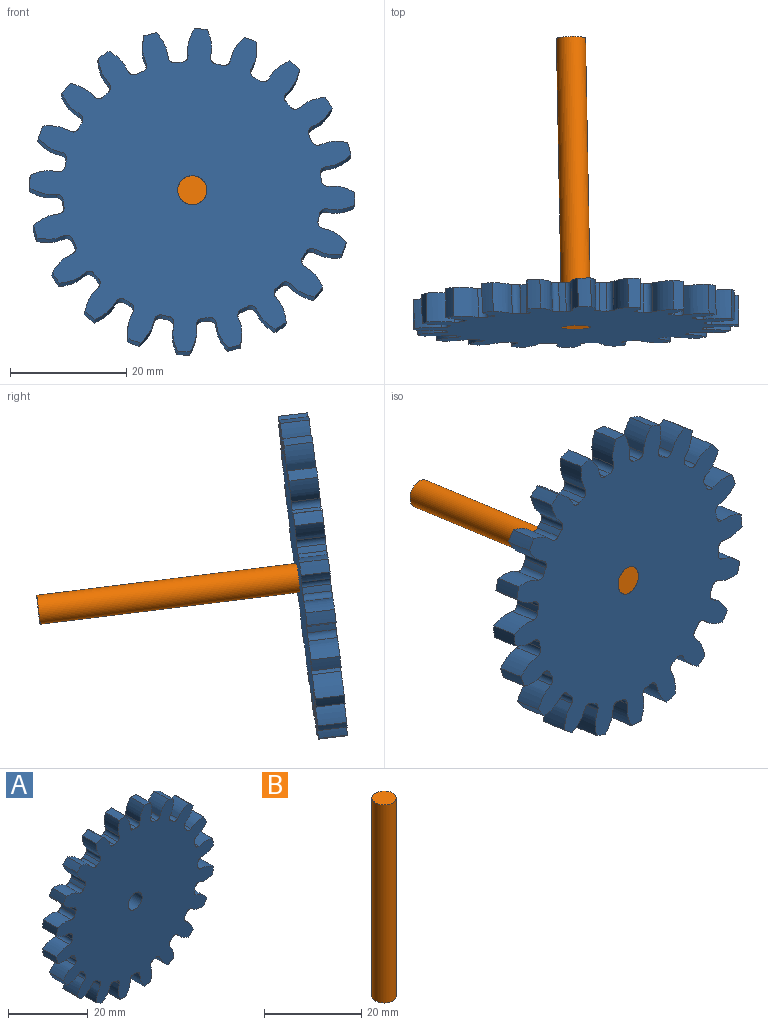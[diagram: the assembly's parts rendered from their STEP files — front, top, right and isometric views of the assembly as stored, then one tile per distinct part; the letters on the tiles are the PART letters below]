
ASSEMBLY  parts=2 mates=1
PART A: 123 faces, bbox 55.6x5x55.6 mm
  f0: extruded ~5x4.52mm, area 24.4mm2, adj f80,f81,f82,f83
  f1: cylinder r=22.23mm len=5mm, axis (0,1,0), area 5.9mm2, adj f81,f82,f83,f84
  f2: extruded ~5x4.52mm, area 24.4mm2, adj f3,f81,f82,f84
  f3: cylinder r=27.94mm len=5mm, axis (0,1,0), area 11.2mm2, adj f2,f4,f81,f82
  f4: extruded ~5x4.78mm, area 24.4mm2, adj f3,f81,f82,f85
  f5: cylinder r=22.23mm len=5mm, axis (0,1,0), area 5.9mm2, adj f81,f82,f85,f86
  f6: extruded ~5x3.82mm, area 24.4mm2, adj f7,f81,f82,f86
  f7: cylinder r=27.94mm len=5mm, axis (0,1,0), area 11.2mm2, adj f6,f8,f81,f82
  f8: extruded ~5x4.57mm, area 24.4mm2, adj f7,f81,f82,f87
  f9: cylinder r=22.23mm len=5mm, axis (0,1,0), area 5.9mm2, adj f81,f82,f87,f88
  f10: extruded ~5x3.92mm, area 24.4mm2, adj f11,f81,f82,f88
  f11: cylinder r=27.94mm len=5mm, axis (0,1,0), area 11.2mm2, adj f10,f12,f81,f82
  f12: extruded ~5x3.92mm, area 24.4mm2, adj f11,f81,f82,f89
  f13: cylinder r=22.23mm len=5mm, axis (0,1,0), area 5.9mm2, adj f81,f82,f89,f90
  f14: extruded ~5x4.57mm, area 24.4mm2, adj f15,f81,f82,f90
  f15: cylinder r=27.94mm len=5mm, axis (0,1,0), area 11.2mm2, adj f14,f16,f81,f82
  f16: extruded ~5x3.82mm, area 24.4mm2, adj f15,f81,f82,f91
  f17: cylinder r=22.23mm len=5mm, axis (0,1,0), area 5.9mm2, adj f81,f82,f91,f92
  f18: extruded ~5x4.78mm, area 24.4mm2, adj f19,f81,f82,f92
  f19: cylinder r=27.94mm len=5mm, axis (0,1,0), area 11.2mm2, adj f18,f20,f81,f82
  f20: extruded ~5x4.52mm, area 24.4mm2, adj f19,f81,f82,f93
  f21: cylinder r=22.23mm len=5mm, axis (0,1,0), area 5.9mm2, adj f81,f82,f93,f94
  f22: extruded ~5x4.52mm, area 24.4mm2, adj f23,f81,f82,f94
  f23: cylinder r=27.94mm len=5mm, axis (0,1,0), area 11.2mm2, adj f22,f24,f81,f82
  f24: extruded ~5x4.78mm, area 24.4mm2, adj f23,f81,f82,f95
  f25: cylinder r=22.23mm len=5mm, axis (0,1,0), area 5.9mm2, adj f81,f82,f95,f96
  f26: extruded ~5x3.82mm, area 24.4mm2, adj f27,f81,f82,f96
  f27: cylinder r=27.94mm len=5mm, axis (0,1,0), area 11.2mm2, adj f26,f28,f81,f82
  f28: extruded ~5x4.57mm, area 24.4mm2, adj f27,f81,f82,f97
  f29: cylinder r=22.23mm len=5mm, axis (0,1,0), area 5.9mm2, adj f81,f82,f97,f98
  f30: extruded ~5x3.92mm, area 24.4mm2, adj f31,f81,f82,f98
  f31: cylinder r=27.94mm len=5mm, axis (0,1,0), area 11.2mm2, adj f30,f32,f81,f82
  f32: extruded ~5x3.92mm, area 24.4mm2, adj f31,f81,f82,f99
  f33: cylinder r=22.23mm len=5mm, axis (0,1,0), area 5.9mm2, adj f81,f82,f99,f100
  f34: extruded ~5x4.57mm, area 24.4mm2, adj f35,f81,f82,f100
  f35: cylinder r=27.94mm len=5mm, axis (0,1,0), area 11.2mm2, adj f34,f36,f81,f82
  f36: extruded ~5x3.82mm, area 24.4mm2, adj f35,f81,f82,f101
  f37: cylinder r=22.23mm len=5mm, axis (0,1,0), area 5.9mm2, adj f81,f82,f101,f102
  f38: extruded ~5x4.78mm, area 24.4mm2, adj f39,f81,f82,f102
  f39: cylinder r=27.94mm len=5mm, axis (0,1,0), area 11.2mm2, adj f38,f40,f81,f82
  f40: extruded ~5x4.52mm, area 24.4mm2, adj f39,f81,f82,f103
  f41: cylinder r=22.23mm len=5mm, axis (0,1,0), area 5.9mm2, adj f81,f82,f103,f104
  f42: extruded ~5x4.52mm, area 24.4mm2, adj f43,f81,f82,f104
  f43: cylinder r=27.94mm len=5mm, axis (0,1,0), area 11.2mm2, adj f42,f44,f81,f82
  f44: extruded ~5x4.78mm, area 24.4mm2, adj f43,f81,f82,f105
  f45: cylinder r=22.23mm len=5mm, axis (0,1,0), area 5.9mm2, adj f81,f82,f105,f106
  f46: extruded ~5x3.82mm, area 24.4mm2, adj f47,f81,f82,f106
  f47: cylinder r=27.94mm len=5mm, axis (0,1,0), area 11.2mm2, adj f46,f48,f81,f82
  f48: extruded ~5x4.57mm, area 24.4mm2, adj f47,f81,f82,f107
  f49: cylinder r=22.23mm len=5mm, axis (0,1,0), area 5.9mm2, adj f81,f82,f107,f108
  f50: extruded ~5x3.92mm, area 24.4mm2, adj f51,f81,f82,f108
  f51: cylinder r=27.94mm len=5mm, axis (0,1,0), area 11.2mm2, adj f50,f52,f81,f82
  f52: extruded ~5x3.92mm, area 24.4mm2, adj f51,f81,f82,f109
  f53: cylinder r=22.23mm len=5mm, axis (0,1,0), area 5.9mm2, adj f81,f82,f109,f110
  f54: extruded ~5x4.57mm, area 24.4mm2, adj f55,f81,f82,f110
  f55: cylinder r=27.94mm len=5mm, axis (0,1,0), area 11.2mm2, adj f54,f56,f81,f82
  f56: extruded ~5x3.82mm, area 24.4mm2, adj f55,f81,f82,f111
  f57: cylinder r=22.23mm len=5mm, axis (0,1,0), area 5.9mm2, adj f81,f82,f111,f112
  f58: extruded ~5x4.78mm, area 24.4mm2, adj f59,f81,f82,f112
  f59: cylinder r=27.94mm len=5mm, axis (0,1,0), area 11.2mm2, adj f58,f60,f81,f82
  f60: extruded ~5x4.52mm, area 24.4mm2, adj f59,f81,f82,f113
  f61: cylinder r=22.23mm len=5mm, axis (0,1,0), area 5.9mm2, adj f81,f82,f113,f114
  f62: extruded ~5x4.52mm, area 24.4mm2, adj f63,f81,f82,f114
  f63: cylinder r=27.94mm len=5mm, axis (0,1,0), area 11.2mm2, adj f62,f64,f81,f82
  f64: extruded ~5x4.78mm, area 24.4mm2, adj f63,f81,f82,f115
  f65: cylinder r=22.23mm len=5mm, axis (0,1,0), area 5.9mm2, adj f81,f82,f115,f116
  f66: extruded ~5x3.82mm, area 24.4mm2, adj f67,f81,f82,f116
  f67: cylinder r=27.94mm len=5mm, axis (0,1,0), area 11.2mm2, adj f66,f68,f81,f82
  f68: extruded ~5x4.57mm, area 24.4mm2, adj f67,f81,f82,f117
  f69: cylinder r=22.23mm len=5mm, axis (0,1,0), area 5.9mm2, adj f81,f82,f117,f118
  f70: extruded ~5x3.92mm, area 24.4mm2, adj f71,f81,f82,f118
  f71: cylinder r=27.94mm len=5mm, axis (0,1,0), area 11.2mm2, adj f70,f72,f81,f82
  f72: extruded ~5x3.92mm, area 24.4mm2, adj f71,f81,f82,f119
  f73: cylinder r=22.23mm len=5mm, axis (0,1,0), area 5.9mm2, adj f81,f82,f119,f120
  f74: extruded ~5x4.57mm, area 24.4mm2, adj f75,f81,f82,f120
  f75: cylinder r=27.94mm len=5mm, axis (0,1,0), area 11.2mm2, adj f74,f76,f81,f82
  f76: extruded ~5x3.82mm, area 24.4mm2, adj f75,f81,f82,f121
  f77: cylinder r=22.23mm len=5mm, axis (0,1,0), area 5.9mm2, adj f81,f82,f121,f122
  f78: extruded ~5x4.78mm, area 24.4mm2, adj f80,f81,f82,f122
  f79: cylinder r=2.5mm len=5mm, axis (0,1,0), area 78.5mm2, adj f81,f82
  f80: cylinder r=27.94mm len=5mm, axis (0,1,0), area 11.2mm2, adj f0,f78,f81,f82
  f81: plane 55.58x55.58mm, normal (0,-1,0), area 1957.9mm2, adj f0,f1,f2,f3,f4,f5,f6,f7
  f82: plane 55.58x55.58mm, normal (0,1,0), area 1957.9mm2, adj f0,f1,f2,f3,f4,f5,f6,f7
  f83: cylinder r=1.09mm len=5mm, axis (0,1,0), area 8.3mm2, adj f0,f1,f81,f82
  f84: cylinder r=1.09mm len=5mm, axis (0,1,0), area 8.3mm2, adj f1,f2,f81,f82
  f85: cylinder r=1.09mm len=5mm, axis (0,1,0), area 8.3mm2, adj f4,f5,f81,f82
  f86: cylinder r=1.09mm len=5mm, axis (0,1,0), area 8.3mm2, adj f5,f6,f81,f82
  f87: cylinder r=1.09mm len=5mm, axis (0,1,0), area 8.3mm2, adj f8,f9,f81,f82
  f88: cylinder r=1.09mm len=5mm, axis (0,1,0), area 8.3mm2, adj f9,f10,f81,f82
  f89: cylinder r=1.09mm len=5mm, axis (0,1,0), area 8.3mm2, adj f12,f13,f81,f82
  f90: cylinder r=1.09mm len=5mm, axis (0,1,0), area 8.3mm2, adj f13,f14,f81,f82
  f91: cylinder r=1.09mm len=5mm, axis (0,1,0), area 8.3mm2, adj f16,f17,f81,f82
  f92: cylinder r=1.09mm len=5mm, axis (0,1,0), area 8.3mm2, adj f17,f18,f81,f82
  f93: cylinder r=1.09mm len=5mm, axis (0,1,0), area 8.3mm2, adj f20,f21,f81,f82
  f94: cylinder r=1.09mm len=5mm, axis (0,1,0), area 8.3mm2, adj f21,f22,f81,f82
  f95: cylinder r=1.09mm len=5mm, axis (0,1,0), area 8.3mm2, adj f24,f25,f81,f82
  f96: cylinder r=1.09mm len=5mm, axis (0,1,0), area 8.3mm2, adj f25,f26,f81,f82
  f97: cylinder r=1.09mm len=5mm, axis (0,1,0), area 8.3mm2, adj f28,f29,f81,f82
  f98: cylinder r=1.09mm len=5mm, axis (0,1,0), area 8.3mm2, adj f29,f30,f81,f82
  f99: cylinder r=1.09mm len=5mm, axis (0,1,0), area 8.3mm2, adj f32,f33,f81,f82
  f100: cylinder r=1.09mm len=5mm, axis (0,1,0), area 8.3mm2, adj f33,f34,f81,f82
  f101: cylinder r=1.09mm len=5mm, axis (0,1,0), area 8.3mm2, adj f36,f37,f81,f82
  f102: cylinder r=1.09mm len=5mm, axis (0,1,0), area 8.3mm2, adj f37,f38,f81,f82
  f103: cylinder r=1.09mm len=5mm, axis (0,1,0), area 8.3mm2, adj f40,f41,f81,f82
  f104: cylinder r=1.09mm len=5mm, axis (0,1,0), area 8.3mm2, adj f41,f42,f81,f82
  f105: cylinder r=1.09mm len=5mm, axis (0,1,0), area 8.3mm2, adj f44,f45,f81,f82
  f106: cylinder r=1.09mm len=5mm, axis (0,1,0), area 8.3mm2, adj f45,f46,f81,f82
  f107: cylinder r=1.09mm len=5mm, axis (0,1,0), area 8.3mm2, adj f48,f49,f81,f82
  f108: cylinder r=1.09mm len=5mm, axis (0,1,0), area 8.3mm2, adj f49,f50,f81,f82
  f109: cylinder r=1.09mm len=5mm, axis (0,1,0), area 8.3mm2, adj f52,f53,f81,f82
  f110: cylinder r=1.09mm len=5mm, axis (0,1,0), area 8.3mm2, adj f53,f54,f81,f82
  f111: cylinder r=1.09mm len=5mm, axis (0,1,0), area 8.3mm2, adj f56,f57,f81,f82
  f112: cylinder r=1.09mm len=5mm, axis (0,1,0), area 8.3mm2, adj f57,f58,f81,f82
  f113: cylinder r=1.09mm len=5mm, axis (0,1,0), area 8.3mm2, adj f60,f61,f81,f82
  f114: cylinder r=1.09mm len=5mm, axis (0,1,0), area 8.3mm2, adj f61,f62,f81,f82
  f115: cylinder r=1.09mm len=5mm, axis (0,1,0), area 8.3mm2, adj f64,f65,f81,f82
  f116: cylinder r=1.09mm len=5mm, axis (0,1,0), area 8.3mm2, adj f65,f66,f81,f82
  f117: cylinder r=1.09mm len=5mm, axis (0,1,0), area 8.3mm2, adj f68,f69,f81,f82
  f118: cylinder r=1.09mm len=5mm, axis (0,1,0), area 8.3mm2, adj f69,f70,f81,f82
  f119: cylinder r=1.09mm len=5mm, axis (0,1,0), area 8.3mm2, adj f72,f73,f81,f82
  f120: cylinder r=1.09mm len=5mm, axis (0,1,0), area 8.3mm2, adj f73,f74,f81,f82
  f121: cylinder r=1.09mm len=5mm, axis (0,1,0), area 8.3mm2, adj f76,f77,f81,f82
  f122: cylinder r=1.09mm len=5mm, axis (0,1,0), area 8.3mm2, adj f77,f78,f81,f82
PART B: 3 faces, bbox 5x5x50 mm
  f0: cylinder r=2.5mm len=50mm, axis (0,0,-1), area 785.4mm2, adj f1,f2
  f1: plane 5x5mm, normal (0,0,1), area 19.6mm2, adj f0
  f2: plane 5x5mm, normal (0,0,-1), area 19.6mm2, adj f0
PLACE A rot(axis=(-0.03,1,-0.06),138.1deg) t=(22.75,27.92,-21.89)mm
PLACE B rot(axis=(-1,-0.01,0.01),97deg) t=(22.84,22.96,-21.28)mm fixed
MATE revolute A.f3 <-> B.f0  axis (-0.02,0.99,-0.12) through (22.84,22.96,-21.28)mm
